FCSTD DOCUMENT  (FreeCAD 0.17R13125 (Git))
Label: cargo_box
License: All rights reserved
LicenseURL: http://en.wikipedia.org/wiki/All_rights_reserved
objects: Sketcher::SketchObject×1
note: 1 computed .brp shape members not serialized (recipe doc carries the construction recipe); baked Part::Feature solids carry a one-line shape summary decoded from their .brp

FEATURE [Sketcher::SketchObject] Sketch
  sketch-geometry (12):
    g0: LineSegment StartX=0 StartY=381 StartZ=0 EndX=600 EndY=381 EndZ=0
    g1: LineSegment StartX=600 StartY=381 StartZ=0 EndX=600 EndY=0 EndZ=0
    g2: LineSegment StartX=600 StartY=0 StartZ=0 EndX=0 EndY=0 EndZ=0
    g3: LineSegment StartX=0 StartY=0 StartZ=0 EndX=0 EndY=381 EndZ=0
    g4: LineSegment StartX=0 StartY=1064.06 StartZ=0 EndX=600 EndY=1064.06 EndZ=0
    g5: LineSegment StartX=600 StartY=1064.06 StartZ=0 EndX=600 EndY=1814.06 EndZ=0
    g6: LineSegment StartX=600 StartY=1814.06 StartZ=0 EndX=0 EndY=1814.06 EndZ=0
    g7: LineSegment StartX=0 StartY=1814.06 StartZ=0 EndX=0 EndY=1064.06 EndZ=0
    g8: LineSegment StartX=-25.0343 StartY=691.491 StartZ=0 EndX=990.966 EndY=691.491 EndZ=0
    g9: LineSegment StartX=990.966 StartY=691.491 StartZ=0 EndX=990.966 EndY=-19.7092 EndZ=0
    g10: LineSegment StartX=990.966 StartY=-19.7092 StartZ=0 EndX=-25.0343 EndY=-19.7092 EndZ=0
    g11: LineSegment StartX=-25.0343 StartY=-19.7092 StartZ=0 EndX=-25.0343 EndY=691.491 EndZ=0
  constraints (33):
    c: Coincident(g0,g1)
    c: Coincident(g1,g2)
    c: Coincident(g2,g3)
    c: Coincident(g3,g0)
    c: Horizontal(g0)
    c: Horizontal(g2)
    c: Vertical(g1)
    c: Vertical(g3)
    c: Coincident(g4,g5)
    c: Coincident(g5,g6)
    c: Coincident(g6,g7)
    c: Coincident(g7,g4)
    c: Horizontal(g4)
    c: Horizontal(g6)
    c: Vertical(g5)
    c: Vertical(g7)
    c: Equal(g4,g0)
    c: Coincident(g2,g-1)
    c: PointOnObject(g4,g-2)
    c: Distance(g5) = 750
    c: Distance(g2) = 600
    c: Distance(g1) = 381
    c: Coincident(g8,g9)
    c: Coincident(g9,g10)
    c: Coincident(g10,g11)
    c: Coincident(g11,g8)
    c: Horizontal(g8)
    c: Horizontal(g10)
    c: Vertical(g9)
    c: Vertical(g11)
    c: Distance(g9) = 711.2
    c: Distance(g10) = 1016
    c: DistanceY(g0,g8) = 310.491
